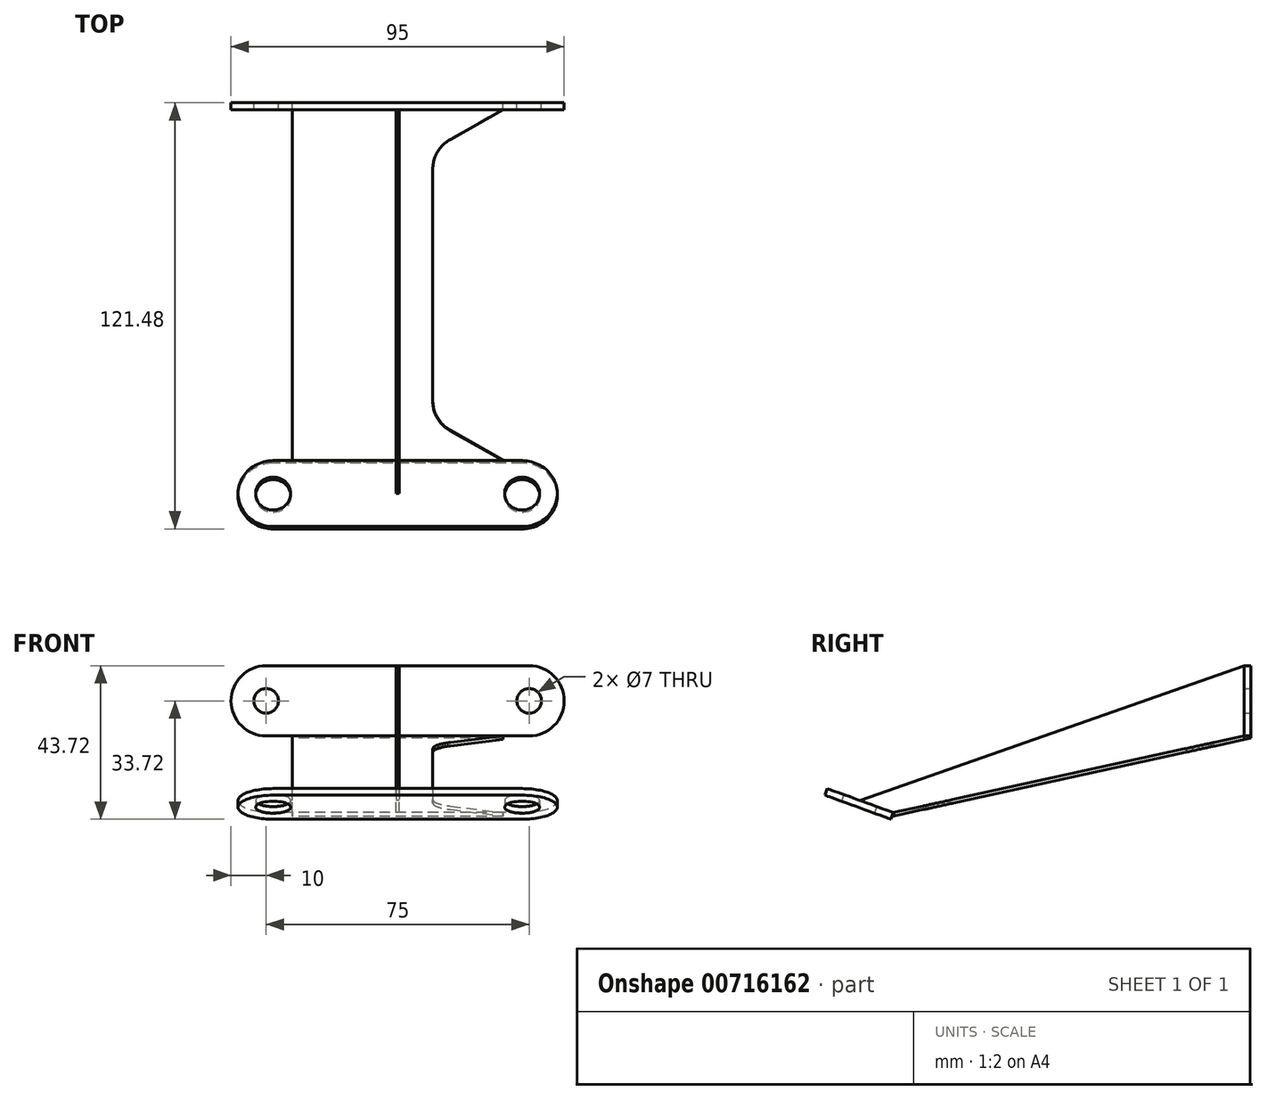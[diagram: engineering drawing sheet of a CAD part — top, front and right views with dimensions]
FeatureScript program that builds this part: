
annotation { "Feature Type Name" : "Feature", "Feature Type Description" : "" }
export const myFeature = defineFeature(function(context is Context, id is Id, definition is map)
    precondition{}
    {
        {
            var Q0;
            Q0=qCreatedBy(makeId("Front.planeOp"),FACE);
            var sketch = newSketch(context, id + "F0", { "sketchPlane" : qUnion([Q0])});
            skLineSegment(sketch, "E0", {"start": v(-37.5, 10) * mm, "end": v(37.5, 10) * mm});
            skArc(sketch, "E1", {"start": v(37.5, -10) * mm, "mid": v(47.5, 0) * mm, "end": v(37.5, 10) * mm});
            skLineSegment(sketch, "E2", {"start": v(37.5, -10) * mm, "end": v(-37.5, -10) * mm});
            skArc(sketch, "E3", {"start": v(-37.5, 10) * mm, "mid": v(-47.5, 0) * mm, "end": v(-37.5, -10) * mm});
            skLineSegment(sketch, "E4", {"start": v(0, 10) * mm, "end": v(0, -10) * mm, "construction": true});
            skCircle(sketch, "E5", {"center": v(-37.5, 0) * mm, "radius": 3.5 * mm});
            skCircle(sketch, "E6", {"center": v(37.5, 0) * mm, "radius": 3.5 * mm});
            skSolve(sketch);
        }
        {
            var Q0;
            Q0 = qSketchRegion(id + "F0", true);
            extrude(context, id + "F1", {"entities" : qUnion([Q0]), "depth" : 2 * mm, "offsetDistance" : 25.4 * mm});
        }
        {
            var Q0;
            Q0=qCreatedBy(makeId("Right.planeOp"),FACE);
            var sketch = newSketch(context, id + "F2", { "sketchPlane" : qUnion([Q0])});
            skLineSegment(sketch, "E7", {"start": v(-102, -31.84) * mm, "end": v(-120.8, -25) * mm});
            skLineSegment(sketch, "E8", {"start": v(-120.8, -25) * mm, "end": v(-121.48, -26.88) * mm});
            skLineSegment(sketch, "E9", {"start": v(-121.48, -26.88) * mm, "end": v(-102.68, -33.72) * mm});
            skLineSegment(sketch, "E10", {"start": v(-102.68, -33.72) * mm, "end": v(-102, -31.84) * mm});
            skLineSegment(sketch, "E11", {"start": v(-102, -31.84) * mm, "end": v(-2, -10) * mm});
            skLineSegment(sketch, "E12.0", {"start": v(-2, -10) * mm, "end": v(-2, 10) * mm});
            skLineSegment(sketch, "E13", {"start": v(-2, 10) * mm, "end": v(-111.4, -28.42) * mm});
            skSolve(sketch);
        }
        {
            var Q0;
            Q0=makeQuery(id+"F2.imprint","IMPRINT",FACE,{"disambiguationData":[TD([[makeQuery(id+"F2.imprint","IMPRINT",EDGE,{"derivedFrom":sQuery(id+"F2.wireOp",EDGE,"E7")}),-1.0]])]});
            extrude(context, id + "F3", {"entities" : qUnion([Q0]), "endBound" : BoundingType.SYMMETRIC, "depth" : 1 * mm, "offsetDistance" : 25 * mm});
        }
        {
            var Q0;
            Q0=makeQuery(id+"F2.imprint","IMPRINT",FACE,{"disambiguationData":[TD([[makeQuery(id+"F2.imprint","IMPRINT",EDGE,{"derivedFrom":sQuery(id+"F2.wireOp",EDGE,"E7")}),1.0]])]});
            extrude(context, id + "F4", {"entities" : qUnion([Q0]), "endBound" : BoundingType.SYMMETRIC, "depth" : 91 * mm, "offsetDistance" : 25 * mm});
        }
        {
            var Q0;
            Q0=makeQuery(id+"F4.opExtrude","CAP_EDGE",EDGE,{"disambiguationData":[OSD([sQuery(id+"F2.wireOp",EDGE,"E8")])],"isStart":false});
            var Q1;
            Q1=makeQuery(id+"F4.opExtrude","CAP_EDGE",EDGE,{"disambiguationData":[OSD([sQuery(id+"F2.wireOp",EDGE,"E10")])],"isStart":false});
            var Q2;
            Q2=makeQuery(id+"F4.opExtrude","CAP_EDGE",EDGE,{"disambiguationData":[OSD([sQuery(id+"F2.wireOp",EDGE,"E8")])],"isStart":true});
            var Q3;
            Q3=makeQuery(id+"F4.opExtrude","CAP_EDGE",EDGE,{"disambiguationData":[OSD([sQuery(id+"F2.wireOp",EDGE,"E10")])],"isStart":true});
            fillet(context, id + "F5", {"entities" : qUnion([Q0, Q1, Q2, Q3]), "radius" : 10 * mm, "tangentPropagation" : true, "allowEdgeOverflow" : false});
        }
        {
            var Q0;
            Q0=makeQuery(id+"F4.opExtrude","SWEPT_FACE",FACE,{"disambiguationData":[OSD([sQuery(id+"F2.wireOp",EDGE,"E9")])]});
            var sketch = newSketch(context, id + "F6", { "sketchPlane" : qUnion([Q0])});
            skPoint(sketch, "E14", {"position": v(35.5, 94.96) * mm});
            skPoint(sketch, "E15", {"position": v(-35.5, 94.96) * mm});
            skSolve(sketch);
        }
        {
            var Q0;
            Q0=sQuery(id+"F6.wireOp",VERTEX,"E14");
            var Q1;
            Q1=sQuery(id+"F6.wireOp",VERTEX,"E15");
            var Q2;
            Q2=makeQuery(id+"F4.opExtrude","SWEPT_BODY",BODY,{"disambiguationData":[OSD([sQuery(id+"F2.wireOp",EDGE,"E7"),sQuery(id+"F2.wireOp",EDGE,"E8"),sQuery(id+"F2.wireOp",EDGE,"E9"),sQuery(id+"F2.wireOp",EDGE,"E10")])]});
            hole(context, id + "F7", {"style" : HoleStyle.SIMPLE, "endStyle" : HoleEndStyle.THROUGH, "holeDiameter" : 10 * mm, "majorDiameter" : 5 * mm, "isTappedThrough" : true, "tappedDepth" : 12 * mm, "tapClearance" : 3, "locations" : qUnion([Q0, Q1]), "scope" : qUnion([Q2])});
        }
        {
            var Q0;
            Q0=qCreatedBy(makeId("Right.planeOp"),FACE);
            var sketch = newSketch(context, id + "F8", { "sketchPlane" : qUnion([Q0])});
            skLineSegment(sketch, "E16.0", {"start": v(-102, -31.84) * mm, "end": v(-2, -10) * mm});
            skLineSegment(sketch, "E16.1", {"start": v(-102, -31.84) * mm, "end": v(-102.4, -32.95) * mm});
            skLineSegment(sketch, "E16.2", {"start": v(-2, -10) * mm, "end": v(0, -10) * mm});
            skLineSegment(sketch, "E17", {"start": v(-102.4, -32.95) * mm, "end": v(0, -10.59) * mm});
            skPoint(sketch, "E18.orphan", {"position": v(-102.68, -33.72) * mm});
            skLineSegment(sketch, "E19", {"start": v(0, -10.59) * mm, "end": v(0, -10) * mm});
            skSolve(sketch);
        }
        {
            var Q0;
            Q0=makeQuery(id+"F8.imprint","IMPRINT",FACE,{"disambiguationData":[TD([[makeQuery(id+"F8.imprint","IMPRINT",EDGE,{"derivedFrom":sQuery(id+"F8.wireOp",EDGE,"E16.0")}),-1.0]])]});
            extrude(context, id + "F9", {"entities" : qUnion([Q0]), "endBound" : BoundingType.SYMMETRIC, "depth" : 60 * mm, "offsetDistance" : 25 * mm});
        }
        {
            var Q0;
            Q0=makeQuery(id+"F9.opExtrude","SWEPT_FACE",FACE,{"disambiguationData":[OSD([sQuery(id+"F8.wireOp",EDGE,"E16.0")])]});
            var sketch = newSketch(context, id + "F10", { "sketchPlane" : qUnion([Q0])});
            skLineSegment(sketch, "E20", {"start": v(30, -4.09) * mm, "end": v(10, -15.63) * mm});
            skLineSegment(sketch, "E21", {"start": v(10, -15.63) * mm, "end": v(10, -94.9) * mm});
            skLineSegment(sketch, "E22", {"start": v(10, -94.9) * mm, "end": v(30, -106.44) * mm});
            skLineSegment(sketch, "E23", {"start": v(30, -106.44) * mm, "end": v(30, -4.09) * mm});
            skSolve(sketch);
        }
        {
            var Q0;
            Q0=makeQuery(id+"F10.imprint","IMPRINT",FACE,{"disambiguationData":[TD([[makeQuery(id+"F10.imprint","IMPRINT",EDGE,{"derivedFrom":sQuery(id+"F10.wireOp",EDGE,"E20")}),1.0]])]});
            extrude(context, id + "F11", {"entities" : qUnion([Q0]), "operationType" : NewBodyOperationType.REMOVE, "endBound" : BoundingType.THROUGH_ALL, "oppositeDirection" : true, "depth" : 25 * mm, "offsetDistance" : 25 * mm});
        }
        {
            var Q0;
            Q0=makeQuery(id+"F11.boolean.opBoolean","COPY",EDGE,{"derivedFrom":makeQuery(id+"F11.opExtrude","SWEPT_EDGE",EDGE,{"disambiguationData":[OSD([sQuery(id+"F10.wireOp",EDGE,"E21"),sQuery(id+"F10.wireOp",EDGE,"E22")])]})});
            var Q1;
            Q1=makeQuery(id+"F11.boolean.opBoolean","COPY",EDGE,{"derivedFrom":makeQuery(id+"F11.opExtrude","SWEPT_EDGE",EDGE,{"disambiguationData":[OSD([sQuery(id+"F10.wireOp",EDGE,"E20"),sQuery(id+"F10.wireOp",EDGE,"E21")])]})});
            var Q2;
            Q2=makeQuery(id+"Fjhj0ah4KSaXIpF_4.1.F11.boolean.opBoolean","COPY",EDGE,{"derivedFrom":makeQuery(id+"Fjhj0ah4KSaXIpF_4.1.F11.opExtrude","SWEPT_EDGE",EDGE,{"disambiguationData":[OSD([sQuery(id+"F10.wireOp",EDGE,"E20"),sQuery(id+"F10.wireOp",EDGE,"E21")])]})});
            var Q3;
            Q3=makeQuery(id+"Fjhj0ah4KSaXIpF_4.1.F11.boolean.opBoolean","COPY",EDGE,{"derivedFrom":makeQuery(id+"Fjhj0ah4KSaXIpF_4.1.F11.opExtrude","SWEPT_EDGE",EDGE,{"disambiguationData":[OSD([sQuery(id+"F10.wireOp",EDGE,"E21"),sQuery(id+"F10.wireOp",EDGE,"E22")])]})});
            fillet(context, id + "F12", {"entities" : qUnion([Q0, Q1, Q2, Q3]), "radius" : 10 * mm, "tangentPropagation" : true, "allowEdgeOverflow" : false});
        }
    });
